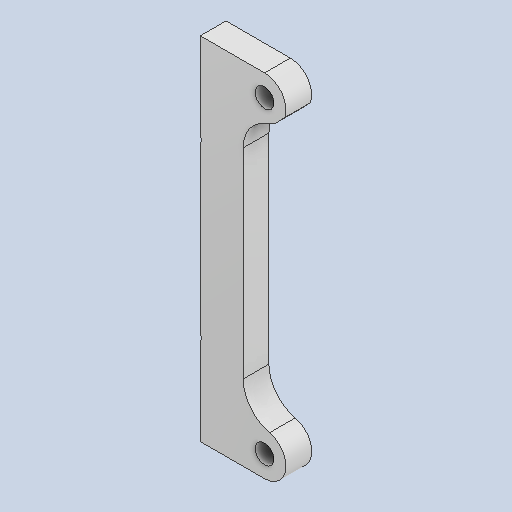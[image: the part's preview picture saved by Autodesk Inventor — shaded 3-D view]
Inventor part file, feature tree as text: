
AUTODESK INVENTOR PART (.ipt)
format: ipt  version: 2025.1 (Build 291241000, 241)  size: 273,920 bytes
history: native  units: mm
features: other x4, fillet x3, sketch x3, extrude x2, reference x2, hole x1, projected_geometry x1
ambient origin geometry x8: Origin, YZ Plane, XZ Plane, XY Plane, X Axis, Y Axis, Z Axis, Center Point
bodies: Body1 (feature_tree)
feature tree (16):
  other  "ソリッド1"
  extrude  "押し出し1"  Depth=2.2mm
  fillet  "フィレット1"  Radius=2.2mm
  hole  "穴1"  [1 undecoded]
  extrude  "押し出し2"  Depth=5.0mm
  fillet  "フィレット2"  Radius=2.0mm
  fillet  "フィレット3"  Radius=10.0mm
  sketch  "スケッチ1"
  reference  "参照1"
  reference  "参照2"
  sketch  "スケッチ2"
  sketch  "スケッチ3"
  projected_geometry  "投影ループ1"
  other  "Assembly1"
  other  "KRS2500_scale:6"
  other  "02157_SmallDiameterHornB:5"
note: 1 required parameter value undecoded (feature->parameter linkage not recoverable at this tier; creation-order binding heuristic only, values carry confidence <= 0.55)
